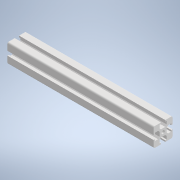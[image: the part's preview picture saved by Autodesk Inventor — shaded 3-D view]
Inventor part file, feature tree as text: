
AUTODESK INVENTOR PART (.ipt)
format: ipt  version: 2020.2 (Build 242310000, 310)  size: 175,104 bytes
history: native  units: in
note: dims shown in document units (in); Inventor stores cm internally (conversion verified against a paired STEP export)
features: extrude x1, sketch x1
ambient origin geometry x8: Origin, YZ Plane, XZ Plane, XY Plane, X Axis, Y Axis, Z Axis, Center Point
bodies: Solid1 (feature_tree)
feature tree (2):
  extrude  "Extrusion1"  Depth=0.29in
  sketch  "Sketch2"  dims[d9=0.2325in d18=0.055in d20=0.055in d34=0.29in d35=0.055in d37=0.058in d38=0.1225in d39=0.081in d40=135.0deg d41=0.17in d42=0.081in d43=0.058in d44=0.055in d45=0.75in d46=0.055in d47=1.5748in d49=360.0deg d51=0.2348in d52=0.232in d56=0.75in d58=0.125in d61=0.055in d62=0.055in d63=0.055in d64=0.055in d65=1.5748in d67=360.0deg d69=5.8in d70=0.0in d71=0.1225in]
